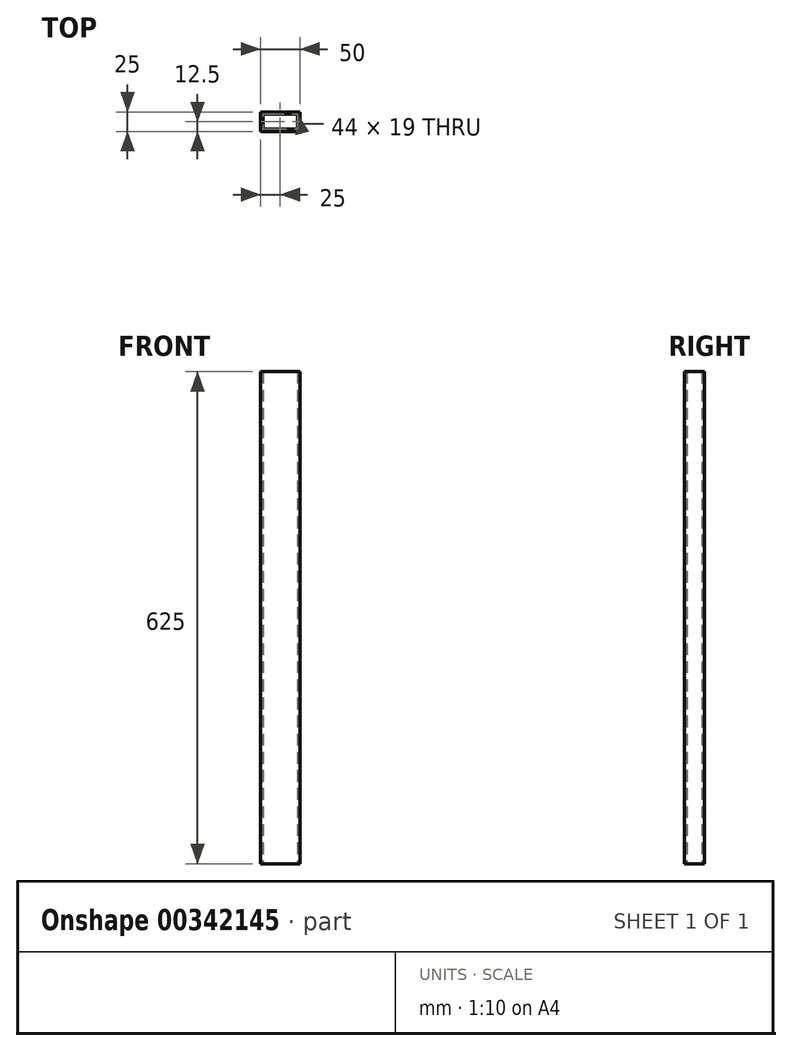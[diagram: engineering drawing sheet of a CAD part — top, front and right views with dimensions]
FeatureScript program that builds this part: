
annotation { "Feature Type Name" : "Feature", "Feature Type Description" : "" }
export const myFeature = defineFeature(function(context is Context, id is Id, definition is map)
    precondition{}
    {
        {
            var Q0;
            Q0=qCreatedBy(makeId("Top.planeOp"),FACE);
            var sketch = newSketch(context, id + "F0", { "sketchPlane" : qUnion([Q0])});
            skLineSegment(sketch, "E0.bottom", {"start": v(-25, -12.5) * mm, "end": v(25, -12.5) * mm});
            skLineSegment(sketch, "E0.top", {"start": v(-25, 12.5) * mm, "end": v(25, 12.5) * mm});
            skLineSegment(sketch, "E0.left", {"start": v(-25, -12.5) * mm, "end": v(-25, 12.5) * mm});
            skLineSegment(sketch, "E0.right", {"start": v(25, -12.5) * mm, "end": v(25, 12.5) * mm});
            skPoint(sketch, "E0.middle", {"position": v(0, 0) * mm});
            skLineSegment(sketch, "E1.bottom", {"start": v(-22, -9.5) * mm, "end": v(22, -9.5) * mm});
            skLineSegment(sketch, "E1.top", {"start": v(-22, 9.5) * mm, "end": v(22, 9.5) * mm});
            skLineSegment(sketch, "E1.left", {"start": v(-22, -9.5) * mm, "end": v(-22, 9.5) * mm});
            skLineSegment(sketch, "E1.right", {"start": v(22, -9.5) * mm, "end": v(22, 9.5) * mm});
            skSolve(sketch);
        }
        {
            var Q0;
            Q0=makeQuery(id+"F0.imprint","IMPRINT",FACE,{"disambiguationData":[TD([[makeQuery(id+"F0.imprint","IMPRINT",EDGE,{"derivedFrom":sQuery(id+"F0.wireOp",EDGE,"E0.bottom")}),1.0]])]});
            extrude(context, id + "F1", {"entities" : qUnion([Q0]), "endBound" : BoundingType.SYMMETRIC, "depth" : 625 * mm});
        }
    });
